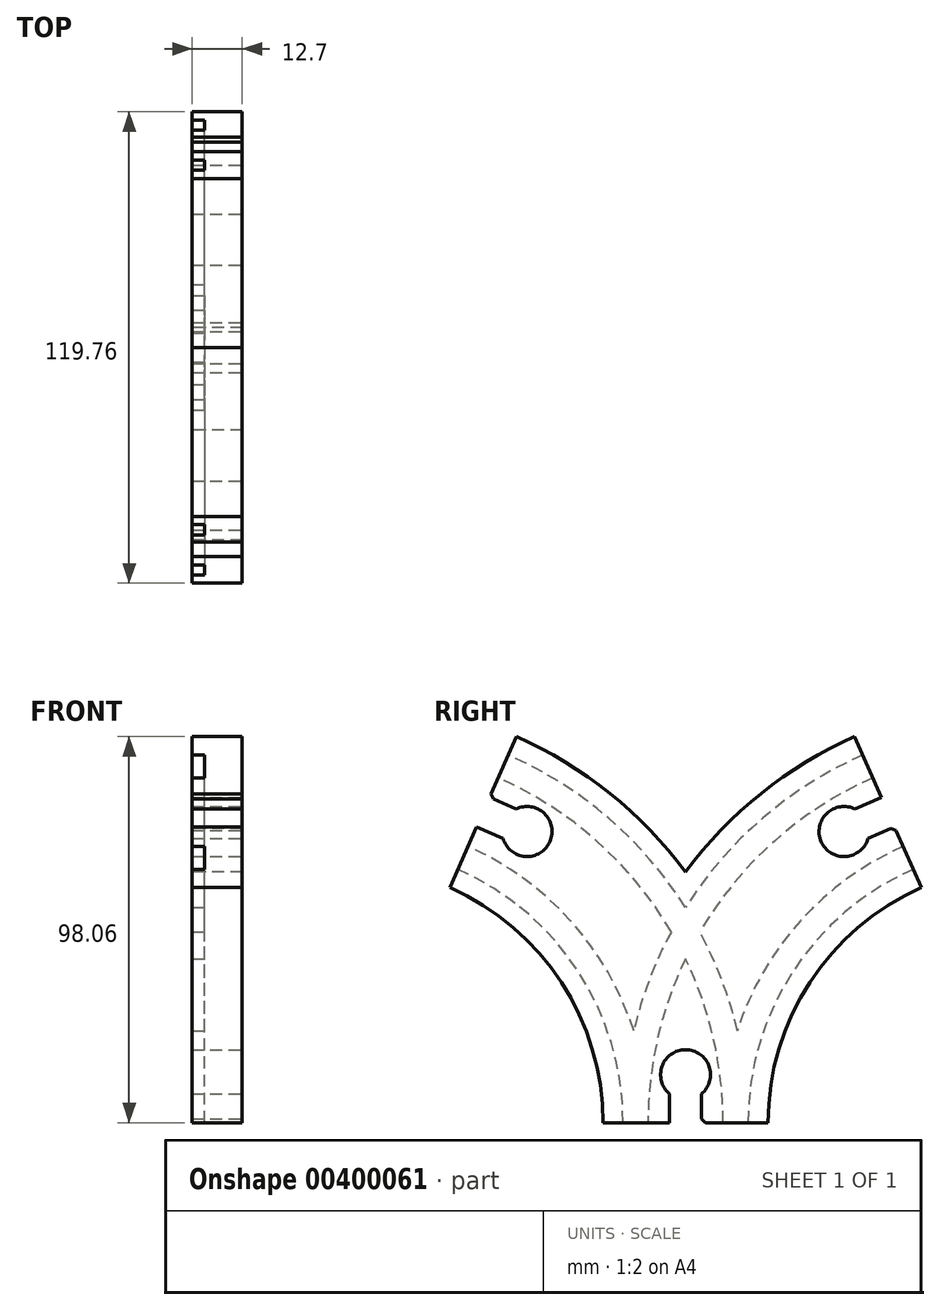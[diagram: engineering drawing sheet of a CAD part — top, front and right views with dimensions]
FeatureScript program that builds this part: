
annotation { "Feature Type Name" : "Feature", "Feature Type Description" : "" }
export const myFeature = defineFeature(function(context is Context, id is Id, definition is map)
    precondition{}
    {
        {
            var Q0;
            Q0=qCreatedBy(makeId("Top.planeOp"),FACE);
            var sketch = newSketch(context, id + "F0", { "sketchPlane" : qUnion([Q0])});
            skLineSegment(sketch, "E0", {"start": v(-2.98, -20.96) * mm, "end": v(-2.98, -15.88) * mm});
            skLineSegment(sketch, "E1", {"start": v(-2.98, -15.88) * mm, "end": v(0.2, -15.88) * mm});
            skLineSegment(sketch, "E2", {"start": v(0.2, -15.88) * mm, "end": v(0.2, -9.53) * mm});
            skLineSegment(sketch, "E3", {"start": v(0.2, -9.53) * mm, "end": v(-2.98, -9.53) * mm});
            skLineSegment(sketch, "E4", {"start": v(-2.98, -9.52) * mm, "end": v(-2.98, 9.52) * mm});
            skLineSegment(sketch, "E5", {"start": v(-2.98, 9.53) * mm, "end": v(0.2, 9.53) * mm});
            skLineSegment(sketch, "E6", {"start": v(0.2, 9.53) * mm, "end": v(0.2, 15.88) * mm});
            skLineSegment(sketch, "E7", {"start": v(0.2, 15.88) * mm, "end": v(-2.98, 15.88) * mm});
            skLineSegment(sketch, "E8", {"start": v(-2.98, 15.88) * mm, "end": v(-2.98, 20.96) * mm});
            skLineSegment(sketch, "E9", {"start": v(-2.98, 20.96) * mm, "end": v(9.72, 20.96) * mm});
            skLineSegment(sketch, "E10", {"start": v(9.72, 20.96) * mm, "end": v(9.72, -20.96) * mm});
            skLineSegment(sketch, "E11", {"start": v(9.72, -20.96) * mm, "end": v(-2.98, -20.96) * mm});
            skLineSegment(sketch, "E12", {"start": v(9.72, 0) * mm, "end": v(-14.33, 0) * mm, "construction": true});
            skSolve(sketch);
        }
        {
            var Q0;
            Q0=qCreatedBy(makeId("Right.planeOp"),FACE);
            var sketch = newSketch(context, id + "F1", { "sketchPlane" : qUnion([Q0])});
            skArc(sketch, "E13", {"start": v(0, 0) * mm, "mid": v(-13.99, 47.08) * mm, "end": v(-51.42, 78.89) * mm});
            skLineSegment(sketch, "E14", {"start": v(0, 0) * mm, "end": v(0, 24.38) * mm, "construction": true});
            skSolve(sketch);
        }
        {
            var Q0;
            Q0=qSketchRegion(id+"F0",true);
            var Q1;
            Q1=sQuery(id+"F1.wireOp",EDGE,"E13");
            sweep(context, id + "F2", {"profiles" : qUnion([Q0]), "path" : qUnion([Q1])});
        }
        {
            var Q0;
            Q0=makeQuery(id+"F2.opSweep","SWEPT_FACE",FACE,{"disambiguationData":[OSD([sQuery(id+"F0.wireOp",EDGE,"E10"),sQuery(id+"F1.wireOp",EDGE,"E13")])]});
            var sketch = newSketch(context, id + "F3", { "sketchPlane" : qUnion([Q0])});
            skLineSegment(sketch, "E15", {"start": v(-51.42, 78.89) * mm, "end": v(-35.14, 71.7) * mm, "construction": true});
            skLineSegment(sketch, "E16", {"start": v(0, 0) * mm, "end": v(0, 26.47) * mm, "construction": true});
            skPoint(sketch, "E16.endSnap0", {"position": v(0, 0) * mm});
            skLineSegment(sketch, "E17", {"start": v(-4.06, 0) * mm, "end": v(-4.06, 7.31) * mm});
            skLineSegment(sketch, "E18", {"start": v(4.06, 0) * mm, "end": v(4.06, 7.31) * mm});
            skArc(sketch, "E19", {"start": v(4.06, 7.31) * mm, "mid": v(0, 18.54) * mm, "end": v(-4.06, 7.31) * mm});
            skLineSegment(sketch, "E20", {"start": v(-4.06, 0) * mm, "end": v(4.06, 0) * mm});
            skLineSegment(sketch, "E21", {"start": v(-49.78, 82.6) * mm, "end": v(-43.09, 79.65) * mm});
            skLineSegment(sketch, "E22", {"start": v(-53.06, 75.17) * mm, "end": v(-46.37, 72.22) * mm});
            skArc(sketch, "E23", {"start": v(-46.37, 72.22) * mm, "mid": v(-34.45, 71.4) * mm, "end": v(-43.09, 79.65) * mm});
            skLineSegment(sketch, "E24", {"start": v(-49.78, 82.6) * mm, "end": v(-53.06, 75.17) * mm});
            skSolve(sketch);
        }
        {
            var Q0;
            Q0=qSketchRegion(id+"F3",true);
            extrude(context, id + "F4", {"entities" : qUnion([Q0]), "operationType" : NewBodyOperationType.REMOVE, "endBound" : BoundingType.UP_TO_NEXT, "oppositeDirection" : true, "depth" : 25.4 * mm});
        }
        {
            var Q0;
            Q0=makeQuery(id+"F4.boolean.opBoolean","COPY",EDGE,{"derivedFrom":makeQuery(id+"F4.opExtrude","SWEPT_EDGE",EDGE,{"disambiguationData":[OSD([sQuery(id+"F0.wireOp",EDGE,"E10"),sQuery(id+"F1.wireOp",VERTEX,"E13.end"),sQuery(id+"F3.wireOp",EDGE,"E22"),sQuery(id+"F3.wireOp",EDGE,"E24")])]})});
            var Q1;
            Q1=makeQuery(id+"F4.boolean.opBoolean","COPY",EDGE,{"derivedFrom":makeQuery(id+"F4.opExtrude","SWEPT_EDGE",EDGE,{"disambiguationData":[OSD([sQuery(id+"F0.wireOp",EDGE,"E10"),sQuery(id+"F1.wireOp",VERTEX,"E13.end"),sQuery(id+"F3.wireOp",EDGE,"E21"),sQuery(id+"F3.wireOp",EDGE,"E24")])]})});
            var Q2;
            Q2=makeQuery(id+"F4.boolean.opBoolean","COPY",EDGE,{"derivedFrom":makeQuery(id+"F4.opExtrude","SWEPT_EDGE",EDGE,{"disambiguationData":[OSD([sQuery(id+"F0.wireOp",EDGE,"E10"),sQuery(id+"F1.wireOp",VERTEX,"E13.start"),sQuery(id+"F3.wireOp",EDGE,"E18"),sQuery(id+"F3.wireOp",EDGE,"E20")])]})});
            var Q3;
            Q3=makeQuery(id+"F4.boolean.opBoolean","COPY",EDGE,{"derivedFrom":makeQuery(id+"F4.opExtrude","SWEPT_EDGE",EDGE,{"disambiguationData":[OSD([sQuery(id+"F0.wireOp",EDGE,"E10"),sQuery(id+"F1.wireOp",VERTEX,"E13.start"),sQuery(id+"F3.wireOp",EDGE,"E17"),sQuery(id+"F3.wireOp",EDGE,"E20")])]})});
            chamfer(context, id + "F5", {"entities" : qUnion([Q0, Q1, Q2, Q3]), "width" : 1.02 * mm, "tangentPropagation" : true});
        }
        {
            var Q0;
            Q0=qCreatedBy(makeId("Right.planeOp"),FACE);
            var sketch = newSketch(context, id + "F6", { "sketchPlane" : qUnion([Q0])});
            skArc(sketch, "E25", {"start": v(51.42, 78.89) * mm, "mid": v(13.99, 47.08) * mm, "end": v(0, 0) * mm});
            skLineSegment(sketch, "E26", {"start": v(0, 0) * mm, "end": v(0, 37.77) * mm, "construction": true});
            skLineSegment(sketch, "E27", {"start": v(-59.88, 59.72) * mm, "end": v(-42.96, 98.06) * mm, "construction": true});
            skLineSegment(sketch, "E28", {"start": v(-51.42, 78.89) * mm, "end": v(51.42, 78.89) * mm, "construction": true});
            skSolve(sketch);
        }
        {
            var Q0;
            Q0 = qSketchRegion(id + "F0", true);
            var Q1;
            Q1=sQuery(id+"F6.wireOp",EDGE,"E25");
            sweep(context, id + "F7", {"operationType" : NewBodyOperationType.ADD, "profiles" : qUnion([Q0]), "path" : qUnion([Q1])});
        }
        {
            var Q0;
            {var subQ0=sQuery(id+"F0.wireOp",EDGE,"E11");var subQ1=sQuery(id+"F0.wireOp",EDGE,"E10");var subQ2=sQuery(id+"F0.wireOp",EDGE,"E9");var subQ3=sQuery(id+"F0.wireOp",EDGE,"E8");var subQ4=sQuery(id+"F0.wireOp",EDGE,"E7");var subQ5=sQuery(id+"F0.wireOp",EDGE,"E6");var subQ6=sQuery(id+"F0.wireOp",EDGE,"E5");var subQ7=sQuery(id+"F0.wireOp",EDGE,"E4");var subQ8=sQuery(id+"F0.wireOp",EDGE,"E3");var subQ9=sQuery(id+"F0.wireOp",EDGE,"E2");var subQ10=sQuery(id+"F0.wireOp",EDGE,"E1");var subQ11=sQuery(id+"F0.wireOp",EDGE,"E0");var subQ15=makeQuery(id+"F2.opSweep","CAP_FACE",FACE,{"disambiguationData":[OSD([subQ11,subQ10,subQ9,subQ8,subQ7,subQ6,subQ5,subQ4,subQ3,subQ2,subQ1,subQ0,sQuery(id+"F1.wireOp",VERTEX,"E13.start")])],"isStart":true});Q0=makeQuery(id+"F7.boolean.opBoolean","MERGE",FACE,{"derivedFrom":[makeQuery(id+"F4.boolean.opBoolean","SPLIT",FACE,{"disambiguationData":[TD([makeQuery(id+"F4.opExtrude","SWEPT_FACE",FACE,{"disambiguationData":[OSD([sQuery(id+"F3.wireOp",EDGE,"E17")])]})])],"derivedFrom":subQ15}),makeQuery(id+"F4.boolean.opBoolean","SPLIT",FACE,{"disambiguationData":[TD([makeQuery(id+"F4.opExtrude","SWEPT_FACE",FACE,{"disambiguationData":[OSD([sQuery(id+"F3.wireOp",EDGE,"E18")])]})])],"derivedFrom":subQ15}),makeQuery(id+"F7.opSweep","CAP_FACE",FACE,{"disambiguationData":[OSD([subQ11,subQ10,subQ9,subQ8,subQ7,subQ6,subQ5,subQ4,subQ3,subQ2,subQ1,subQ0,sQuery(id+"F6.wireOp",VERTEX,"E25.end")])],"isStart":true})]});}
            var sketch = newSketch(context, id + "F8", { "sketchPlane" : qUnion([Q0])});
            skLineSegment(sketch, "E29.bottom", {"start": v(-2.98, -15.88) * mm, "end": v(0.2, -15.88) * mm});
            skLineSegment(sketch, "E29.top", {"start": v(-2.98, -9.53) * mm, "end": v(0.2, -9.53) * mm});
            skLineSegment(sketch, "E29.left", {"start": v(-2.98, -15.88) * mm, "end": v(-2.98, -9.53) * mm});
            skLineSegment(sketch, "E29.right", {"start": v(0.2, -15.88) * mm, "end": v(0.2, -9.53) * mm});
            skLineSegment(sketch, "E30.bottom", {"start": v(-2.98, 9.53) * mm, "end": v(0.2, 9.53) * mm});
            skLineSegment(sketch, "E30.top", {"start": v(-2.98, 15.88) * mm, "end": v(0.2, 15.88) * mm});
            skLineSegment(sketch, "E30.left", {"start": v(-2.98, 9.53) * mm, "end": v(-2.98, 15.88) * mm});
            skLineSegment(sketch, "E30.right", {"start": v(0.2, 9.53) * mm, "end": v(0.2, 15.88) * mm});
            skSolve(sketch);
        }
        {
            var Q0;
            Q0 = qSketchRegion(id + "F8", true);
            var Q1;
            Q1=makeQuery(id+"F7.opSweep","SWEPT_EDGE",EDGE,{"disambiguationData":[OSD([sQuery(id+"F0.wireOp",EDGE,"E8"),sQuery(id+"F0.wireOp",EDGE,"E9"),sQuery(id+"F6.wireOp",EDGE,"E25")])]});
            sweep(context, id + "F9", {"operationType" : NewBodyOperationType.REMOVE, "profiles" : qUnion([Q0]), "path" : qUnion([Q1])});
        }
        {
            var Q0;
            Q0 = qSketchRegion(id + "F8", true);
            var Q1;
            Q1=makeQuery(id+"F2.opSweep","SWEPT_EDGE",EDGE,{"disambiguationData":[OSD([sQuery(id+"F0.wireOp",EDGE,"E0"),sQuery(id+"F0.wireOp",EDGE,"E11"),sQuery(id+"F1.wireOp",EDGE,"E13")])]});
            sweep(context, id + "F10", {"operationType" : NewBodyOperationType.REMOVE, "profiles" : qUnion([Q0]), "path" : qUnion([Q1])});
        }
        {
            var Q0;
            {var subQ0=sQuery(id+"F0.wireOp",EDGE,"E10");Q0=makeQuery(id+"F7.boolean.opBoolean","MERGE",FACE,{"derivedFrom":[makeQuery(id+"F2.opSweep","SWEPT_FACE",FACE,{"disambiguationData":[OSD([subQ0,sQuery(id+"F1.wireOp",EDGE,"E13")])]}),makeQuery(id+"F7.opSweep","SWEPT_FACE",FACE,{"disambiguationData":[OSD([subQ0,sQuery(id+"F6.wireOp",EDGE,"E25")])]})]});}
            var sketch = newSketch(context, id + "F11", { "sketchPlane" : qUnion([Q0])});
            skLineSegment(sketch, "E31", {"start": v(4.06, 0) * mm, "end": v(4.06, 7.31) * mm});
            skLineSegment(sketch, "E32", {"start": v(0, 0) * mm, "end": v(0, 20.3) * mm, "construction": true});
            skPoint(sketch, "E32.endSnap0", {"position": v(0, 0) * mm});
            skLineSegment(sketch, "E33", {"start": v(-4.06, 0) * mm, "end": v(-4.06, 7.31) * mm});
            skArc(sketch, "E34", {"start": v(4.06, 7.31) * mm, "mid": v(0, 18.54) * mm, "end": v(-4.06, 7.31) * mm});
            skLineSegment(sketch, "E35", {"start": v(51.42, 78.89) * mm, "end": v(39.9, 73.8) * mm, "construction": true});
            skLineSegment(sketch, "E36", {"start": v(53.06, 75.17) * mm, "end": v(46.37, 72.22) * mm});
            skLineSegment(sketch, "E37", {"start": v(49.78, 82.6) * mm, "end": v(43.09, 79.65) * mm});
            skLineSegment(sketch, "E38", {"start": v(49.78, 82.6) * mm, "end": v(53.06, 75.17) * mm});
            skArc(sketch, "E39", {"start": v(43.09, 79.65) * mm, "mid": v(34.45, 71.4) * mm, "end": v(46.37, 72.22) * mm});
            skLineSegment(sketch, "E40", {"start": v(4.06, 0) * mm, "end": v(-4.06, 0) * mm});
            skSolve(sketch);
        }
        {
            var Q0;
            Q0 = qSketchRegion(id + "F11", true);
            extrude(context, id + "F12", {"entities" : qUnion([Q0]), "operationType" : NewBodyOperationType.REMOVE, "endBound" : BoundingType.UP_TO_NEXT, "oppositeDirection" : true, "depth" : 25.4 * mm});
        }
        {
            var Q0;
            Q0=makeQuery(id+"F12.boolean.opBoolean","COPY",EDGE,{"derivedFrom":makeQuery(id+"F12.opExtrude","SWEPT_EDGE",EDGE,{"disambiguationData":[OSD([sQuery(id+"F0.wireOp",EDGE,"E10"),sQuery(id+"F1.wireOp",VERTEX,"E13.start"),sQuery(id+"F6.wireOp",VERTEX,"E25.end"),sQuery(id+"F11.wireOp",EDGE,"E31"),sQuery(id+"F11.wireOp",EDGE,"E40")])]})});
            var Q1;
            Q1=makeQuery(id+"F12.boolean.opBoolean","COPY",EDGE,{"derivedFrom":makeQuery(id+"F12.opExtrude","SWEPT_EDGE",EDGE,{"disambiguationData":[OSD([sQuery(id+"F0.wireOp",EDGE,"E10"),sQuery(id+"F1.wireOp",VERTEX,"E13.start"),sQuery(id+"F6.wireOp",VERTEX,"E25.end"),sQuery(id+"F11.wireOp",EDGE,"E33"),sQuery(id+"F11.wireOp",EDGE,"E40")])]})});
            var Q2;
            Q2=makeQuery(id+"F12.boolean.opBoolean","COPY",EDGE,{"derivedFrom":makeQuery(id+"F12.opExtrude","SWEPT_EDGE",EDGE,{"disambiguationData":[OSD([sQuery(id+"F0.wireOp",EDGE,"E10"),sQuery(id+"F6.wireOp",VERTEX,"E25.start"),sQuery(id+"F11.wireOp",EDGE,"E36"),sQuery(id+"F11.wireOp",EDGE,"E38")])]})});
            var Q3;
            Q3=makeQuery(id+"F12.boolean.opBoolean","COPY",EDGE,{"derivedFrom":makeQuery(id+"F12.opExtrude","SWEPT_EDGE",EDGE,{"disambiguationData":[OSD([sQuery(id+"F0.wireOp",EDGE,"E10"),sQuery(id+"F6.wireOp",VERTEX,"E25.start"),sQuery(id+"F11.wireOp",EDGE,"E37"),sQuery(id+"F11.wireOp",EDGE,"E38")])]})});
            chamfer(context, id + "F13", {"entities" : qUnion([Q0, Q1, Q2, Q3]), "width" : 1.02 * mm, "tangentPropagation" : true});
        }
    });
